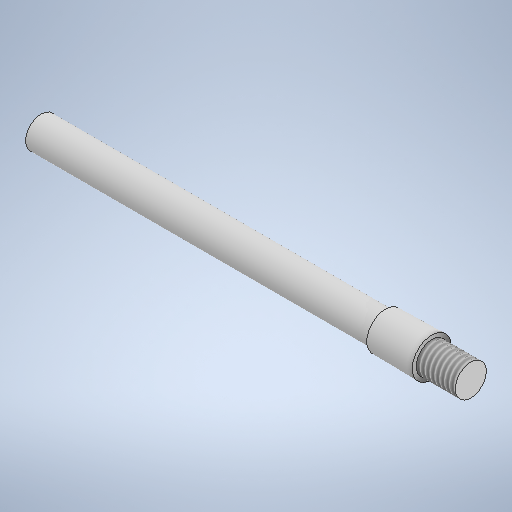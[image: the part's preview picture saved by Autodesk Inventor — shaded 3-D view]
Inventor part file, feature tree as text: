
AUTODESK INVENTOR PART (.ipt)
format: ipt  version: 2025.1 (Build 291241000, 241)  size: 270,848 bytes
history: native  units: mm
features: revolve x1, thread x1, sketch x1
ambient origin geometry x8: Origin, YZ Plane, XZ Plane, XY Plane, X Axis, Y Axis, Z Axis, Center Point
bodies: Volumenkörper1 (feature_tree)
feature tree (3):
  revolve  "Umdrehung1"
  thread  "Gewinde1"  [1 undecoded]
  sketch  "Skizze1"  dims[d2=10.0mm d3=10.0mm d4=12.0mm d5=8.0mm d6=0.174533mm d7=100.0mm d8=17.453293mm d9=90.0deg d10=10.0mm d11=0.0mm]
note: 1 required parameter value undecoded (feature->parameter linkage not recoverable at this tier; creation-order binding heuristic only, values carry confidence <= 0.55)
